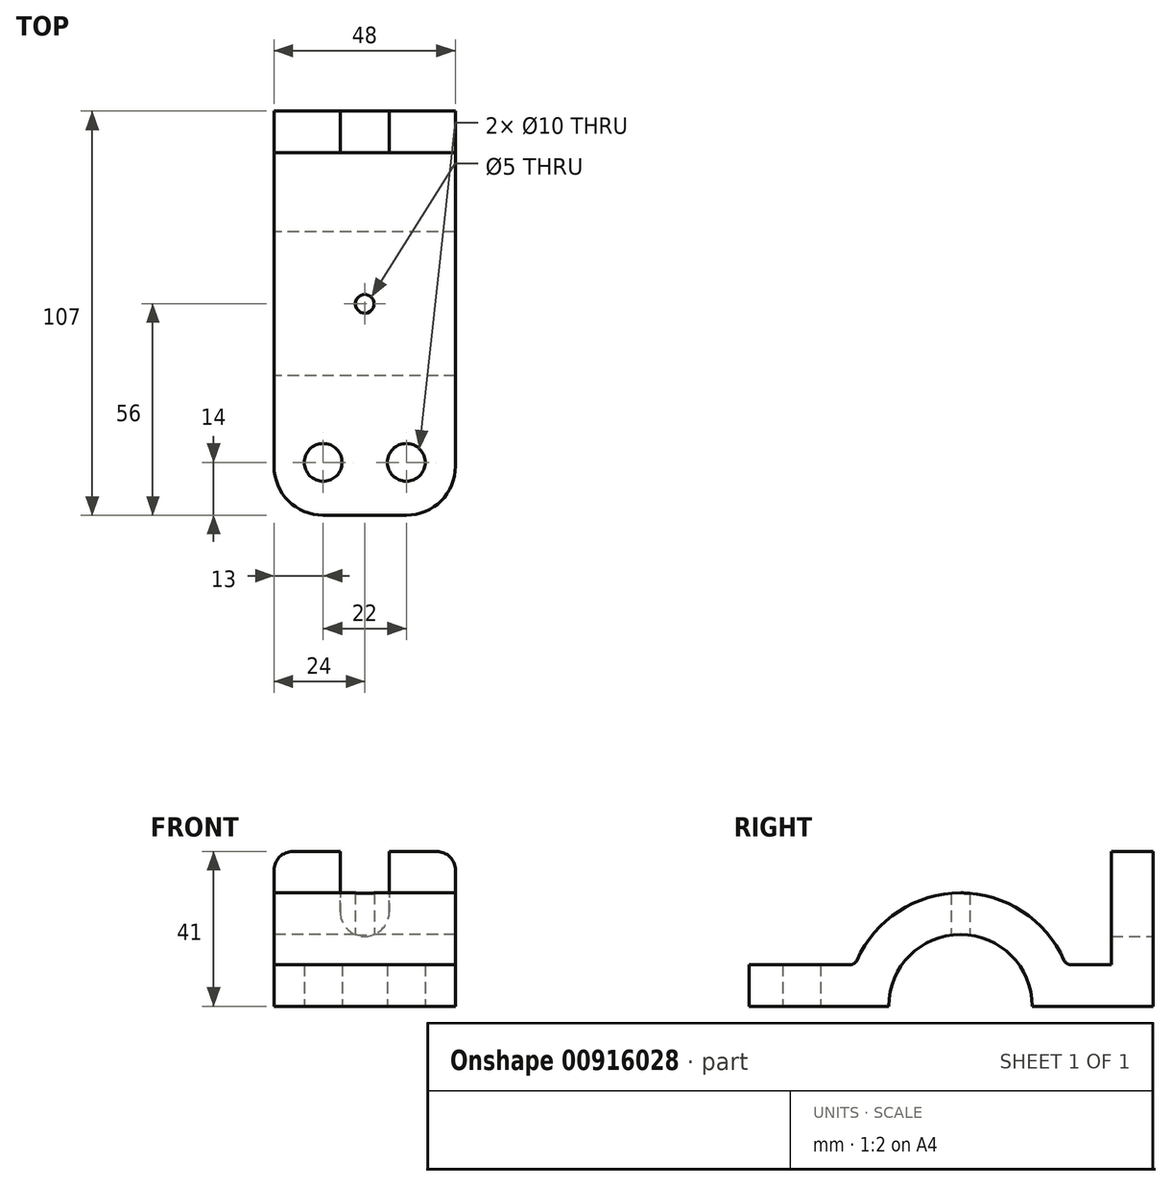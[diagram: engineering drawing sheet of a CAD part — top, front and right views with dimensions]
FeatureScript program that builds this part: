
annotation { "Feature Type Name" : "Feature", "Feature Type Description" : "" }
export const myFeature = defineFeature(function(context is Context, id is Id, definition is map)
    precondition{}
    {
        {
            var Q0;
            Q0=qCreatedBy(makeId("Right.planeOp"),FACE);
            var sketch = newSketch(context, id + "F0", { "sketchPlane" : qUnion([Q0])});
            skLineSegment(sketch, "E0", {"start": v(0, 0) * mm, "end": v(51, 0) * mm});
            skLineSegment(sketch, "E1", {"start": v(51, 0) * mm, "end": v(51, 11) * mm});
            skLineSegment(sketch, "E2", {"start": v(51, 11) * mm, "end": v(-56, 11) * mm});
            skLineSegment(sketch, "E3", {"start": v(-56, 11) * mm, "end": v(-56, 0) * mm});
            skLineSegment(sketch, "E4", {"start": v(-56, 0) * mm, "end": v(0, 0) * mm});
            skCircle(sketch, "E5", {"center": v(0, 0) * mm, "radius": 30 * mm});
            skCircle(sketch, "E6", {"center": v(0, 0) * mm, "radius": 19 * mm});
            skLineSegment(sketch, "E7", {"start": v(51, 0) * mm, "end": v(51, 41) * mm});
            skLineSegment(sketch, "E8", {"start": v(51, 41) * mm, "end": v(40, 41) * mm});
            skLineSegment(sketch, "E9", {"start": v(40, 41) * mm, "end": v(40, 11) * mm});
            skSolve(sketch);
        }
        {
            var Q0;
            {var subQ0=sQuery(id+"F0.wireOp",EDGE,"E3");Q0=makeQuery(id+"F0.imprint","IMPRINT",FACE,{"disambiguationData":[TD([[makeQuery(id+"F0.imprint","IMPRINT",EDGE,{"derivedFrom":subQ0}),1.0]])]});}
            var Q1;
            {var subQ0=sQuery(id+"F0.wireOp",EDGE,"E5");var subQ1=sQuery(id+"F0.wireOp",EDGE,"E2");var subQ2=makeQuery(id+"F0.imprint","INTERSECT",VERTEX,{"disambiguationData":[OD(0.0)],"derivedFrom":[subQ1,subQ0]});Q1=makeQuery(id+"F0.imprint","IMPRINT",FACE,{"disambiguationData":[TD([[makeQuery(id+"F0.imprint","IMPRINT",EDGE,{"disambiguationData":[TD([[subQ2,1.0]])],"derivedFrom":subQ1}),1.0]])]});}
            var Q2;
            {var subQ0=sQuery(id+"F0.wireOp",EDGE,"E6");var subQ1=sQuery(id+"F0.wireOp",EDGE,"E2");var subQ2=makeQuery(id+"F0.imprint","INTERSECT",VERTEX,{"disambiguationData":[OD(0.0)],"derivedFrom":[subQ1,subQ0]});Q2=makeQuery(id+"F0.imprint","IMPRINT",FACE,{"disambiguationData":[TD([[makeQuery(id+"F0.imprint","IMPRINT",EDGE,{"disambiguationData":[TD([[subQ2,1.0]])],"derivedFrom":subQ1}),-1.0]])]});}
            var Q3;
            {var subQ0=sQuery(id+"F0.wireOp",EDGE,"E5");var subQ1=sQuery(id+"F0.wireOp",EDGE,"E0");var subQ2=makeQuery(id+"F0.imprint","INTERSECT",VERTEX,{"derivedFrom":[subQ1,subQ0]});Q3=makeQuery(id+"F0.imprint","IMPRINT",FACE,{"disambiguationData":[TD([[makeQuery(id+"F0.imprint","IMPRINT",EDGE,{"disambiguationData":[TD([[subQ2,1.0]])],"derivedFrom":subQ1}),1.0]])]});}
            var Q4;
            {var subQ1=sQuery(id+"F0.wireOp",EDGE,"E1");Q4=makeQuery(id+"F0.imprint","IMPRINT",FACE,{"disambiguationData":[TD([[makeQuery(id+"F0.imprint","IMPRINT",EDGE,{"derivedFrom":subQ1}),1.0]])]});}
            var Q5;
            {var subQ0=sQuery(id+"F0.wireOp",EDGE,"E7");Q5=makeQuery(id+"F0.imprint","IMPRINT",FACE,{"disambiguationData":[TD([[makeQuery(id+"F0.imprint","IMPRINT",EDGE,{"derivedFrom":subQ0}),1.0]])]});}
            var Q6;
            Q6 = qSketchRegion(id + "F2", true);
            extrude(context, id + "F1", {"entities" : qUnion([Q0, Q1, Q2, Q3, Q4, Q5, Q6]), "endBound" : BoundingType.SYMMETRIC, "depth" : 48 * mm, "offsetDistance" : 25 * mm});
        }
        {
            var Q0;
            Q0=makeQuery(id+"F1.opExtrude","SWEPT_FACE",FACE,{"disambiguationData":[OSD([sQuery(id+"F0.wireOp",EDGE,"E1"),sQuery(id+"F0.wireOp",EDGE,"E7")])]});
            var sketch = newSketch(context, id + "F2", { "sketchPlane" : qUnion([Q0])});
            skLineSegment(sketch, "E10", {"start": v(0, 0) * mm, "end": v(0, 25) * mm, "construction": true});
            skLineSegment(sketch, "E11", {"start": v(0, 41) * mm, "end": v(0, 25) * mm, "construction": true});
            skLineSegment(sketch, "E12", {"start": v(6.5, 41) * mm, "end": v(6.5, 25) * mm});
            skLineSegment(sketch, "E13", {"start": v(-6.5, 41) * mm, "end": v(-6.5, 24.63) * mm});
            skCircle(sketch, "E14", {"center": v(0, 25) * mm, "radius": 6.5 * mm});
            skLineSegment(sketch, "E15", {"start": v(-6.5, 41) * mm, "end": v(6.5, 41) * mm});
            skSolve(sketch);
        }
        {
            var Q0;
            {var subQ0=sQuery(id+"F2.wireOp",EDGE,"E12");Q0=makeQuery(id+"F2.imprint","IMPRINT",FACE,{"disambiguationData":[TD([[makeQuery(id+"F2.imprint","IMPRINT",EDGE,{"derivedFrom":subQ0}),-1.0]])]});}
            var Q1;
            {var subQ0=sQuery(id+"F2.wireOp",EDGE,"E14");var subQ1=makeQuery(id+"F2.imprint","INTERSECT",VERTEX,{"derivedFrom":[sQuery(id+"F2.wireOp",EDGE,"E12"),subQ0]});Q1=makeQuery(id+"F2.imprint","IMPRINT",FACE,{"disambiguationData":[TD([[makeQuery(id+"F2.imprint","IMPRINT",EDGE,{"disambiguationData":[TD([[subQ1,-1.0]])],"derivedFrom":subQ0}),1.0]])]});}
            var Q2;
            Q2=makeQuery(id+"F1.opExtrude","SWEPT_FACE",FACE,{"disambiguationData":[OSD([sQuery(id+"F0.wireOp",EDGE,"E9")])]});
            extrude(context, id + "F3", {"entities" : qUnion([Q0, Q1]), "operationType" : NewBodyOperationType.REMOVE, "endBound" : BoundingType.UP_TO_SURFACE, "oppositeDirection" : true, "depth" : 15.5 * mm, "endBoundEntityFace" : qUnion([Q2]), "offsetDistance" : 25 * mm});
        }
        {
            var Q0;
            Q0=qCreatedBy(makeId("Top.planeOp"),FACE);
            var sketch = newSketch(context, id + "F4", { "sketchPlane" : qUnion([Q0])});
            skPoint(sketch, "E16", {"position": v(0, 0) * mm});
            skLineSegment(sketch, "E17", {"start": v(0, -57.77) * mm, "end": v(0, -14.84) * mm, "construction": true});
            skLineSegment(sketch, "E18", {"start": v(-11, -42) * mm, "end": v(0, -42) * mm});
            skLineSegment(sketch, "E19.MirrorCS", {"start": v(11, -42) * mm, "end": v(0, -42) * mm});
            skPoint(sketch, "E20", {"position": v(-11, -42) * mm});
            skPoint(sketch, "E21", {"position": v(11, -42) * mm});
            skSolve(sketch);
        }
        {
            var Q0;
            Q0=sQuery(id+"F4.wireOp",VERTEX,"E16");
            var Q1;
            Q1=makeQuery(id+"F1.opExtrude","SWEPT_BODY",BODY,{"disambiguationData":[OSD([sQuery(id+"F0.wireOp",EDGE,"E0"),sQuery(id+"F0.wireOp",EDGE,"E1"),sQuery(id+"F0.wireOp",EDGE,"E2"),sQuery(id+"F0.wireOp",EDGE,"E3"),sQuery(id+"F0.wireOp",EDGE,"E4"),sQuery(id+"F0.wireOp",EDGE,"E5"),sQuery(id+"F0.wireOp",EDGE,"E6"),sQuery(id+"F0.wireOp",EDGE,"E7"),sQuery(id+"F0.wireOp",EDGE,"E8"),sQuery(id+"F0.wireOp",EDGE,"E9")])]});
            hole(context, id + "F5", {"style" : HoleStyle.SIMPLE, "endStyle" : HoleEndStyle.THROUGH, "oppositeDirection" : true, "holeDiameter" : 5 * mm, "majorDiameter" : 5 * mm, "isTappedThrough" : true, "tappedDepth" : 12 * mm, "tapClearance" : 3, "locations" : qUnion([Q0]), "scope" : qUnion([Q1])});
        }
        {
            var Q0;
            Q0=sQuery(id+"F4.wireOp",VERTEX,"E20");
            var Q1;
            Q1=sQuery(id+"F4.wireOp",VERTEX,"E21");
            var Q2;
            Q2=makeQuery(id+"F1.opExtrude","SWEPT_BODY",BODY,{"disambiguationData":[OSD([sQuery(id+"F0.wireOp",EDGE,"E0"),sQuery(id+"F0.wireOp",EDGE,"E1"),sQuery(id+"F0.wireOp",EDGE,"E2"),sQuery(id+"F0.wireOp",EDGE,"E3"),sQuery(id+"F0.wireOp",EDGE,"E4"),sQuery(id+"F0.wireOp",EDGE,"E5"),sQuery(id+"F0.wireOp",EDGE,"E6"),sQuery(id+"F0.wireOp",EDGE,"E7"),sQuery(id+"F0.wireOp",EDGE,"E8"),sQuery(id+"F0.wireOp",EDGE,"E9")])]});
            hole(context, id + "F6", {"style" : HoleStyle.SIMPLE, "endStyle" : HoleEndStyle.THROUGH, "oppositeDirection" : true, "holeDiameter" : 10 * mm, "majorDiameter" : 5 * mm, "isTappedThrough" : true, "tappedDepth" : 12 * mm, "tapClearance" : 3, "locations" : qUnion([Q0, Q1]), "scope" : qUnion([Q2])});
        }
        {
            var Q0;
            Q0=makeQuery(id+"F1.opExtrude","CAP_EDGE",EDGE,{"disambiguationData":[OSD([sQuery(id+"F0.wireOp",EDGE,"E3")])],"isStart":true});
            var Q1;
            Q1=makeQuery(id+"F1.opExtrude","CAP_EDGE",EDGE,{"disambiguationData":[OSD([sQuery(id+"F0.wireOp",EDGE,"E3")])],"isStart":false});
            fillet(context, id + "F7", {"entities" : qUnion([Q0, Q1]), "radius" : 13 * mm, "tangentPropagation" : true, "allowEdgeOverflow" : false});
        }
        {
            var Q0;
            Q0=makeQuery(id+"F1.opExtrude","CAP_EDGE",EDGE,{"disambiguationData":[OSD([sQuery(id+"F0.wireOp",EDGE,"E8")])],"isStart":true});
            var Q1;
            Q1=makeQuery(id+"F1.opExtrude","CAP_EDGE",EDGE,{"disambiguationData":[OSD([sQuery(id+"F0.wireOp",EDGE,"E8")])],"isStart":false});
            fillet(context, id + "F8", {"entities" : qUnion([Q0, Q1]), "radius" : 5 * mm, "tangentPropagation" : true, "allowEdgeOverflow" : false});
        }
        {
            var Q0;
            {var subQ0=sQuery(id+"F0.wireOp",EDGE,"E5");var subQ1=sQuery(id+"F0.wireOp",EDGE,"E2");Q0=makeQuery(id+"F1.opExtrude","SWEPT_EDGE",EDGE,{"disambiguationData":[OSD([subQ1,subQ0]),TDD([makeQuery(id+"F0.imprint","INTERSECT",VERTEX,{"disambiguationData":[OD(0.0)],"derivedFrom":[subQ1,subQ0]})])]});}
            var Q1;
            {var subQ0=sQuery(id+"F0.wireOp",EDGE,"E5");var subQ1=sQuery(id+"F0.wireOp",EDGE,"E2");Q1=makeQuery(id+"F1.opExtrude","SWEPT_EDGE",EDGE,{"disambiguationData":[OSD([subQ1,subQ0]),TDD([makeQuery(id+"F0.imprint","INTERSECT",VERTEX,{"disambiguationData":[OD(1.0)],"derivedFrom":[subQ1,subQ0]})])]});}
            fillet(context, id + "F9", {"entities" : qUnion([Q0, Q1]), "radius" : 2 * mm, "tangentPropagation" : true, "allowEdgeOverflow" : false});
        }
    });
